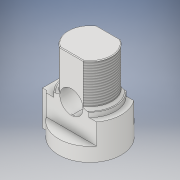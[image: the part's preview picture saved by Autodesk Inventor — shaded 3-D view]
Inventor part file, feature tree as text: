
AUTODESK INVENTOR PART (.ipt)
format: ipt  version: 2019 (Build 230136000, 136)  size: 218,624 bytes
history: native  units: mm
features: sketch x9, extrude x8, thread x3, fillet x2
ambient origin geometry x8: Origin, YZ Plane, XZ Plane, XY Plane, X Axis, Y Axis, Z Axis, Center Point
bodies: Solid1 (feature_tree)
feature tree (22):
  extrude  "Extrusion1"  Depth=14.0mm
  extrude  "Extrusion2"  Depth=22.0mm
  extrude  "Extrusion3"  Depth=19.0mm
  fillet  "Fillet1"  Radius=2.0mm
  extrude  "Extrusion4"  Depth=20.0mm
  extrude  "Extrusion5"  Depth=29.0mm TaperAngle=0.0deg
  extrude  "Extrusion6"  Depth=19.0mm TaperAngle=0.0deg
  extrude  "Extrusion7"  Depth=10.0mm
  thread  "Thread1"  [1 undecoded]
  thread  "Thread2"  [1 undecoded]
  fillet  "Fillet2"  Radius=0.3mm
  thread  "Thread3"  [1 undecoded]
  extrude  "Extrusion8"  Depth=10.0mm TaperAngle=0.0deg
  sketch  "Sketch9"
  sketch  "Sketch1"  dims[d0=27.0mm d2=14.0mm]
  sketch  "Sketch2"  dims[d4=15.0mm d5=0.0mm d6=22.0mm]
  sketch  "Sketch3"  dims[d7=2.0mm d8=0.0mm d9=19.0mm d10=2.0mm d11=0.0mm]
  sketch  "Sketch4"  dims[d12=1.0mm d13=20.0mm]
  sketch  "Sketch5"  dims[d14=16.0mm d15=0.0mm d19=29.0mm d20=0.0mm]
  sketch  "Sketch6"  dims[d21=9.0mm d22=19.0mm d23=0.0mm]
  sketch  "Sketch7"  dims[d24=12.0mm d25=0.0mm d26=15.0mm d27=10.0mm d28=0.0mm d29=10.0mm d30=0.0mm d31=0.3mm d32=10.0mm d33=0.0mm]
  sketch  "Sketch8"  dims[d34=10.0mm d35=20.0mm d36=0.0mm]
note: 3 required parameter values undecoded (feature->parameter linkage not recoverable at this tier; creation-order binding heuristic only, values carry confidence <= 0.55)
